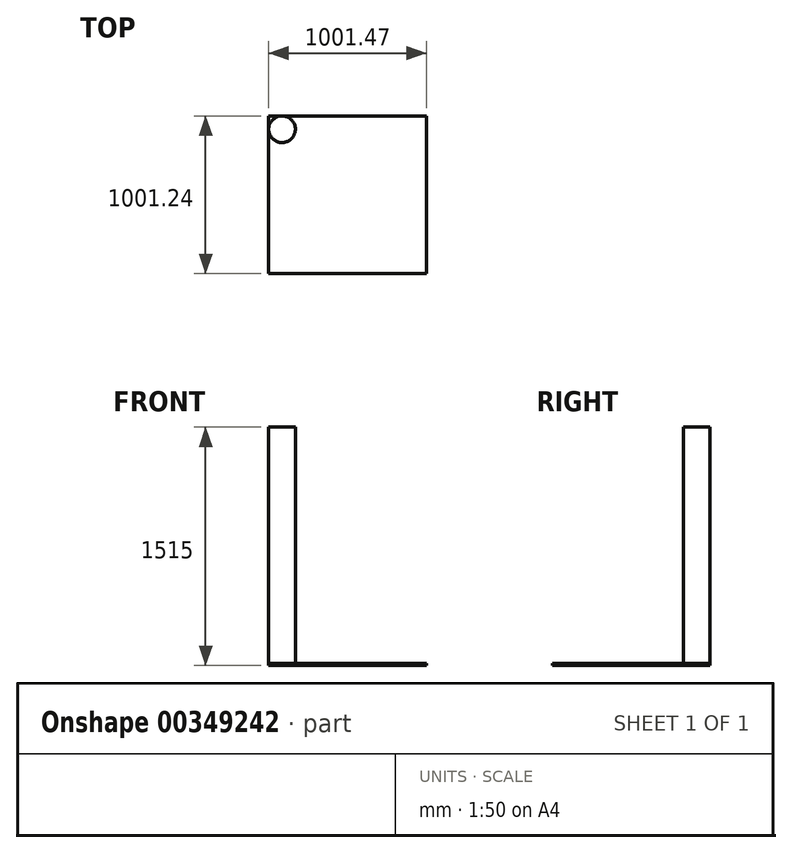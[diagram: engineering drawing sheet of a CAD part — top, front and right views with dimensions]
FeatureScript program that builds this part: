
annotation { "Feature Type Name" : "Feature", "Feature Type Description" : "" }
export const myFeature = defineFeature(function(context is Context, id is Id, definition is map)
    precondition{}
    {
        {
            var Q0;
            Q0=qCreatedBy(makeId("Top.planeOp"),FACE);
            var sketch = newSketch(context, id + "F0", { "sketchPlane" : qUnion([Q0])});
            skLineSegment(sketch, "E0.bottom", {"start": v(-573.3, 393.35) * mm, "end": v(427.69, 393.35) * mm});
            skLineSegment(sketch, "E0.top", {"start": v(-573.3, -607.88) * mm, "end": v(427.69, -607.88) * mm});
            skLineSegment(sketch, "E0.left", {"start": v(-573.3, 393.35) * mm, "end": v(-573.3, -607.88) * mm});
            skLineSegment(sketch, "E0.right", {"start": v(427.69, 393.35) * mm, "end": v(427.69, -607.88) * mm});
            skSolve(sketch);
        }
        {
            var Q0;
            Q0 = qSketchRegion(id + "F0", true);
            extrude(context, id + "F1", {"entities" : qUnion([Q0]), "depth" : 15 * mm});
        }
        {
            var Q0;
            Q0=makeQuery(id+"F1.opExtrude","CAP_FACE",FACE,{"disambiguationData":[OSD([sQuery(id+"F0.wireOp",EDGE,"E0.bottom"),sQuery(id+"F0.wireOp",EDGE,"E0.top"),sQuery(id+"F0.wireOp",EDGE,"E0.left"),sQuery(id+"F0.wireOp",EDGE,"E0.right")])],"isStart":false});
            var sketch = newSketch(context, id + "F2", { "sketchPlane" : qUnion([Q0])});
            skCircle(sketch, "E1", {"center": v(-489.12, 308.7) * mm, "radius": 84.65 * mm});
            skPoint(sketch, "E1.first.point", {"position": v(-573.3, 317.64) * mm});
            skPoint(sketch, "E1.second.point", {"position": v(-405.45, 295.9) * mm});
            skPoint(sketch, "E1.third.point", {"position": v(-487.8, 393.35) * mm});
            skSolve(sketch);
        }
        {
            var Q0;
            Q0 = qSketchRegion(id + "F2", true);
            extrude(context, id + "F3", {"entities" : qUnion([Q0]), "operationType" : NewBodyOperationType.ADD, "depth" : 1500 * mm});
        }
    });
